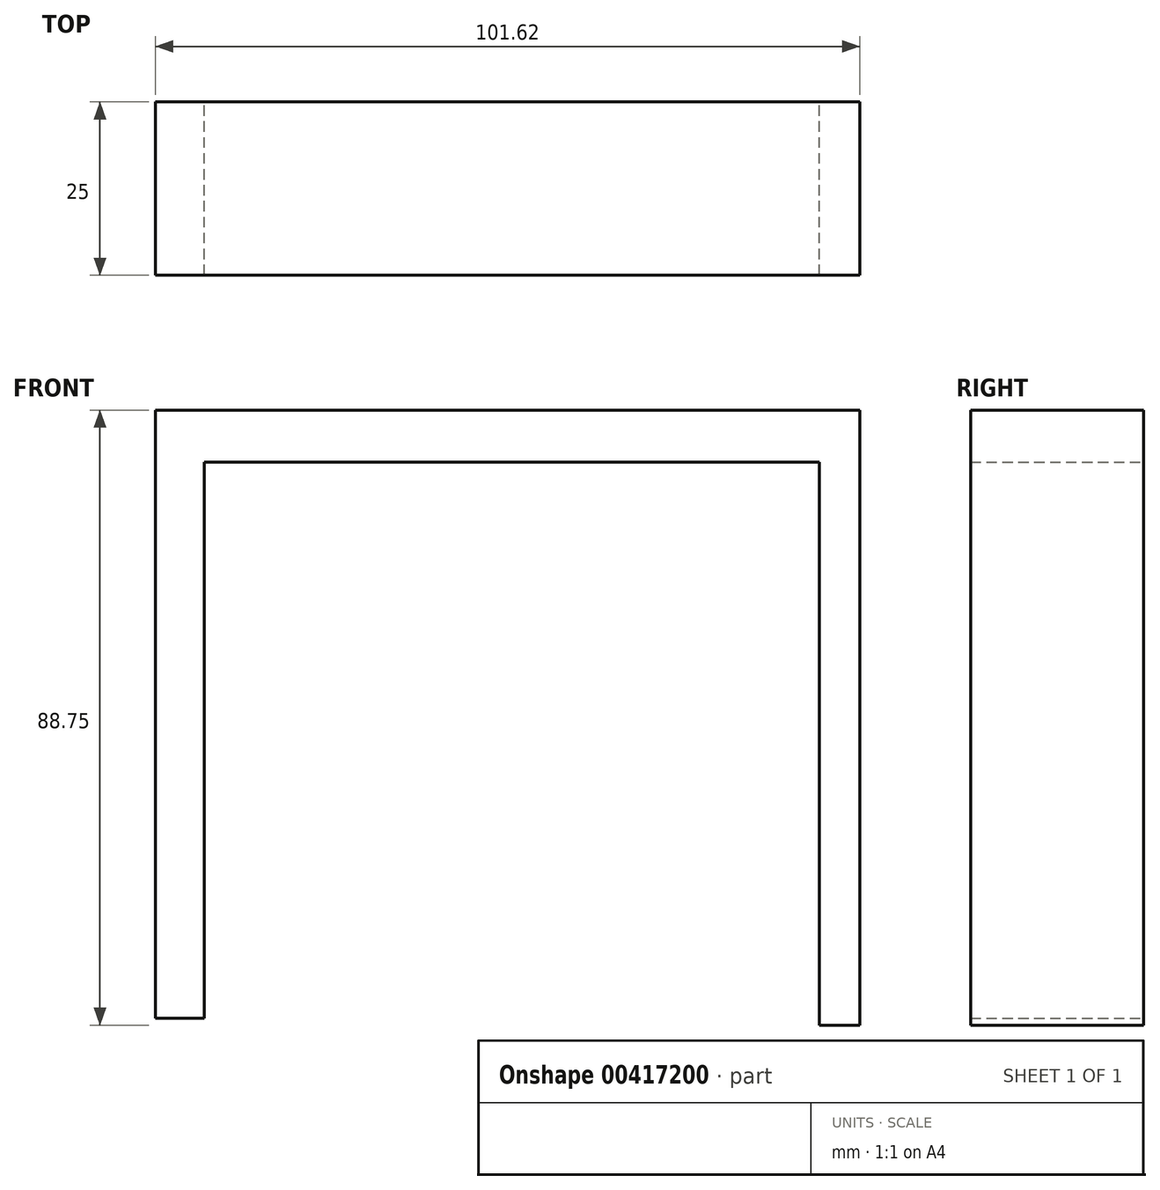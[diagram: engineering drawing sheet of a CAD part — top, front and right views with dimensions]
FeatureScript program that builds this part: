
annotation { "Feature Type Name" : "Feature", "Feature Type Description" : "" }
export const myFeature = defineFeature(function(context is Context, id is Id, definition is map)
    precondition{}
    {
        {
            var Q0;
            Q0=qCreatedBy(makeId("Front.planeOp"),FACE);
            var sketch = newSketch(context, id + "F0", { "sketchPlane" : qUnion([Q0])});
            skLineSegment(sketch, "E0.bottom", {"start": v(-49.88, 42.98) * mm, "end": v(51.74, 42.98) * mm});
            skLineSegment(sketch, "E0.top", {"start": v(-49.88, 35.46) * mm, "end": v(51.74, 35.46) * mm});
            skLineSegment(sketch, "E0.left", {"start": v(-49.88, 42.98) * mm, "end": v(-49.88, 35.46) * mm});
            skLineSegment(sketch, "E0.right", {"start": v(51.74, 42.98) * mm, "end": v(51.74, 35.46) * mm});
            skLineSegment(sketch, "E1.bottom", {"start": v(-49.88, 35.46) * mm, "end": v(-42.86, 35.46) * mm});
            skLineSegment(sketch, "E1.top", {"start": v(-49.88, -44.77) * mm, "end": v(-42.86, -44.77) * mm});
            skLineSegment(sketch, "E1.left", {"start": v(-49.88, 35.46) * mm, "end": v(-49.88, -44.77) * mm});
            skLineSegment(sketch, "E1.right", {"start": v(-42.86, 35.46) * mm, "end": v(-42.86, -44.77) * mm});
            skLineSegment(sketch, "E2.bottom", {"start": v(51.74, 35.46) * mm, "end": v(45.9, 35.46) * mm});
            skLineSegment(sketch, "E2.top", {"start": v(51.74, -45.77) * mm, "end": v(45.9, -45.77) * mm});
            skLineSegment(sketch, "E2.left", {"start": v(51.74, 35.46) * mm, "end": v(51.74, -45.77) * mm});
            skLineSegment(sketch, "E2.right", {"start": v(45.9, 35.46) * mm, "end": v(45.9, -45.77) * mm});
            skSolve(sketch);
        }
        {
            var Q0;
            Q0 = qSketchRegion(id + "F0", true);
            extrude(context, id + "F1", {"entities" : qUnion([Q0]), "depth" : 25 * mm});
        }
    });
